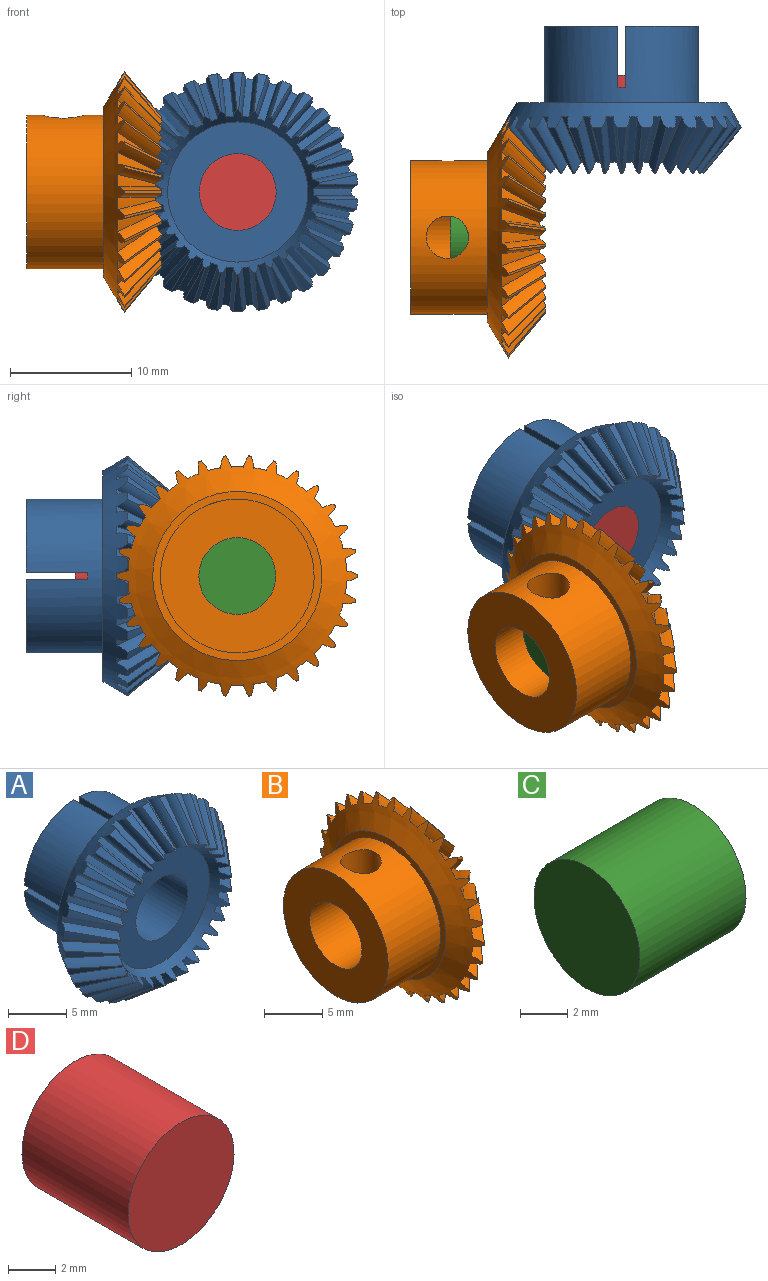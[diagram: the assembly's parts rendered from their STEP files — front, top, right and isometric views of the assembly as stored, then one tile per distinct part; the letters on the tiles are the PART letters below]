
ASSEMBLY  parts=4 mates=2
PART A: 142 faces, bbox 20.3x12.2x20.3 mm
  f0: cone r=8.72mm half-angle=30deg, axis (0,-1,0), area 108.7mm2, adj f4,f8,f9,f10,f11,f12,f13,f14
  f1: cone r=6.8mm half-angle=30deg, axis (0,-1,0), area 49.4mm2, adj f4,f8,f9,f10,f11,f12,f13,f14
  f2: cylinder r=3.17mm len=10.41mm, axis (0,1,0), area 194.7mm2, adj f5,f6,f7,f36,f37,f130,f131,f132
  f3: cylinder r=6.35mm len=12.7mm, axis (0,1,0), area 240.4mm2, adj f5,f6,f7,f36,f39,f130,f131,f132
  f4: cone r=9.91mm half-angle=39.7deg, axis (0,1,0), area 2.1mm2, adj f0,f1,f106,f111
  f5: plane 6.02x6.02mm, normal (0,1,0), area 21.7mm2, adj f2,f3,f137,f139
  f6: plane 6.02x6.02mm, normal (0,1,0), area 21.7mm2, adj f2,f3,f134,f136
  f7: plane 6.02x6.02mm, normal (0,1,0), area 21.7mm2, adj f2,f3,f131,f133
  f8: cone r=9.91mm half-angle=39.7deg, axis (0,1,0), area 2.1mm2, adj f0,f1,f42,f127
  f9: cone r=9.91mm half-angle=39.7deg, axis (0,1,0), area 2.1mm2, adj f0,f1,f124,f129
  f10: cone r=9.91mm half-angle=39.7deg, axis (0,1,0), area 2.1mm2, adj f0,f1,f121,f126
  f11: cone r=9.91mm half-angle=39.7deg, axis (0,1,0), area 2.1mm2, adj f0,f1,f118,f123
  f12: cone r=9.91mm half-angle=39.7deg, axis (0,1,0), area 2.1mm2, adj f0,f1,f115,f120
  f13: cone r=9.91mm half-angle=39.7deg, axis (0,1,0), area 2.1mm2, adj f0,f1,f112,f117
  f14: cone r=9.91mm half-angle=39.7deg, axis (0,1,0), area 2.1mm2, adj f0,f1,f109,f114
  f15: cone r=9.91mm half-angle=39.7deg, axis (0,1,0), area 2.1mm2, adj f0,f1,f103,f108
  f16: cone r=9.91mm half-angle=39.7deg, axis (0,1,0), area 2.1mm2, adj f0,f1,f100,f105
  f17: cone r=9.91mm half-angle=39.7deg, axis (0,1,0), area 2.1mm2, adj f0,f1,f97,f102
  f18: cone r=9.91mm half-angle=39.7deg, axis (0,1,0), area 2.1mm2, adj f0,f1,f94,f99
  f19: cone r=9.91mm half-angle=39.7deg, axis (0,1,0), area 2.1mm2, adj f0,f1,f91,f96
  f20: cone r=9.91mm half-angle=39.7deg, axis (0,1,0), area 2.1mm2, adj f0,f1,f88,f93
  f21: cone r=9.91mm half-angle=39.7deg, axis (0,1,0), area 2.1mm2, adj f0,f1,f85,f90
  f22: cone r=9.91mm half-angle=39.7deg, axis (0,1,0), area 2.1mm2, adj f0,f1,f82,f87
  f23: cone r=9.91mm half-angle=39.7deg, axis (0,1,0), area 2.1mm2, adj f0,f1,f79,f84
  f24: cone r=9.91mm half-angle=39.7deg, axis (0,1,0), area 2.1mm2, adj f0,f1,f76,f81
  f25: cone r=9.91mm half-angle=39.7deg, axis (0,1,0), area 2.1mm2, adj f0,f1,f73,f78
  f26: cone r=9.91mm half-angle=39.7deg, axis (0,1,0), area 2.1mm2, adj f0,f1,f70,f75
  f27: cone r=9.91mm half-angle=39.7deg, axis (0,1,0), area 2.1mm2, adj f0,f1,f67,f72
  f28: cone r=9.91mm half-angle=39.7deg, axis (0,1,0), area 2.1mm2, adj f0,f1,f64,f69
  f29: cone r=9.91mm half-angle=39.7deg, axis (0,1,0), area 2.1mm2, adj f0,f1,f61,f66
  f30: cone r=9.91mm half-angle=39.7deg, axis (0,1,0), area 2.1mm2, adj f0,f1,f58,f63
  f31: cone r=9.91mm half-angle=39.7deg, axis (0,1,0), area 2.1mm2, adj f0,f1,f55,f60
  f32: cone r=9.91mm half-angle=39.7deg, axis (0,1,0), area 2.1mm2, adj f0,f1,f52,f57
  f33: cone r=9.91mm half-angle=39.7deg, axis (0,1,0), area 2.1mm2, adj f0,f1,f49,f54
  f34: cone r=9.91mm half-angle=39.7deg, axis (0,1,0), area 2.1mm2, adj f0,f1,f46,f51
  f35: cone r=9.91mm half-angle=39.7deg, axis (0,1,0), area 2.1mm2, adj f0,f1,f43,f48
  f36: plane 6.02x6.02mm, normal (0,1,0), area 21.7mm2, adj f2,f3,f130,f140
  f37: plane 11.58x11.58mm, normal (0,-1,0), area 73.7mm2, adj f1,f2
  f38: cone r=9.91mm half-angle=39.7deg, axis (0,1,0), area 2.1mm2, adj f0,f1,f41,f45
  f39: plane 17.45x17.45mm, normal (0,1,0), area 112.4mm2, adj f0,f3
  f40: cylinder r=7.38mm len=3.75mm, axis (0.64,-0.77,0), area 3mm2, adj f0,f1,f41,f42
  f41: cylinder r=1.83mm len=4.68mm, axis (0.64,-0.77,0), area 5.2mm2, adj f0,f1,f38,f40
  f42: cylinder r=1.83mm len=4.68mm, axis (0.64,-0.77,0), area 5.2mm2, adj f0,f1,f8,f40
  f43: cylinder r=1.83mm len=4.68mm, axis (0.63,-0.77,0.13), area 5.2mm2, adj f0,f1,f35,f44
  f44: cylinder r=7.38mm len=3.75mm, axis (0.63,-0.77,0.13), area 3mm2, adj f0,f1,f43,f45
  f45: cylinder r=1.83mm len=4.68mm, axis (0.63,-0.77,0.13), area 5.2mm2, adj f0,f1,f38,f44
  f46: cylinder r=1.83mm len=4.68mm, axis (0.58,-0.77,0.26), area 5.2mm2, adj f0,f1,f34,f47
  f47: cylinder r=7.38mm len=3.75mm, axis (0.58,-0.77,0.26), area 3mm2, adj f0,f1,f46,f48
  f48: cylinder r=1.83mm len=4.68mm, axis (0.58,-0.77,0.26), area 5.2mm2, adj f0,f1,f35,f47
  f49: cylinder r=1.83mm len=4.68mm, axis (0.52,-0.77,0.38), area 5.2mm2, adj f0,f1,f33,f50
  f50: cylinder r=7.38mm len=3.75mm, axis (0.52,-0.77,0.38), area 3mm2, adj f0,f1,f49,f51
  f51: cylinder r=1.83mm len=4.68mm, axis (0.52,-0.77,0.38), area 5.2mm2, adj f0,f1,f34,f50
  f52: cylinder r=1.83mm len=4.68mm, axis (0.43,-0.77,0.48), area 5.2mm2, adj f0,f1,f32,f53
  f53: cylinder r=7.38mm len=3.75mm, axis (0.43,-0.77,0.48), area 3mm2, adj f0,f1,f52,f54
  f54: cylinder r=1.83mm len=4.68mm, axis (0.43,-0.77,0.48), area 5.2mm2, adj f0,f1,f33,f53
  f55: cylinder r=1.83mm len=4.68mm, axis (0.32,-0.77,0.55), area 5.2mm2, adj f0,f1,f31,f56
  f56: cylinder r=7.38mm len=3.75mm, axis (0.32,-0.77,0.55), area 3mm2, adj f0,f1,f55,f57
  f57: cylinder r=1.83mm len=4.68mm, axis (0.32,-0.77,0.55), area 5.2mm2, adj f0,f1,f32,f56
  f58: cylinder r=1.83mm len=4.68mm, axis (0.2,-0.77,0.61), area 5.2mm2, adj f0,f1,f30,f59
  f59: cylinder r=7.38mm len=3.75mm, axis (0.2,-0.77,0.61), area 3mm2, adj f0,f1,f58,f60
  f60: cylinder r=1.83mm len=4.68mm, axis (0.2,-0.77,0.61), area 5.2mm2, adj f0,f1,f31,f59
  f61: cylinder r=1.83mm len=4.68mm, axis (0.07,-0.77,0.64), area 5.2mm2, adj f0,f1,f29,f62
  f62: cylinder r=7.38mm len=3.75mm, axis (0.07,-0.77,0.64), area 3mm2, adj f0,f1,f61,f63
  f63: cylinder r=1.83mm len=4.68mm, axis (0.07,-0.77,0.64), area 5.2mm2, adj f0,f1,f30,f62
  f64: cylinder r=1.83mm len=4.68mm, axis (-0.07,-0.77,0.64), area 5.2mm2, adj f0,f1,f28,f65
  f65: cylinder r=7.38mm len=3.75mm, axis (-0.07,-0.77,0.64), area 3mm2, adj f0,f1,f64,f66
  f66: cylinder r=1.83mm len=4.68mm, axis (-0.07,-0.77,0.64), area 5.2mm2, adj f0,f1,f29,f65
  f67: cylinder r=1.83mm len=4.68mm, axis (-0.2,-0.77,0.61), area 5.2mm2, adj f0,f1,f27,f68
  f68: cylinder r=7.38mm len=3.75mm, axis (-0.2,-0.77,0.61), area 3mm2, adj f0,f1,f67,f69
  f69: cylinder r=1.83mm len=4.68mm, axis (-0.2,-0.77,0.61), area 5.2mm2, adj f0,f1,f28,f68
  f70: cylinder r=1.83mm len=4.68mm, axis (-0.32,-0.77,0.55), area 5.2mm2, adj f0,f1,f26,f71
  f71: cylinder r=7.38mm len=3.75mm, axis (-0.32,-0.77,0.55), area 3mm2, adj f0,f1,f70,f72
  f72: cylinder r=1.83mm len=4.68mm, axis (-0.32,-0.77,0.55), area 5.2mm2, adj f0,f1,f27,f71
  f73: cylinder r=1.83mm len=4.68mm, axis (-0.43,-0.77,0.48), area 5.2mm2, adj f0,f1,f25,f74
  f74: cylinder r=7.38mm len=3.75mm, axis (-0.43,-0.77,0.48), area 3mm2, adj f0,f1,f73,f75
  f75: cylinder r=1.83mm len=4.68mm, axis (-0.43,-0.77,0.48), area 5.2mm2, adj f0,f1,f26,f74
  f76: cylinder r=1.83mm len=4.68mm, axis (-0.52,-0.77,0.38), area 5.2mm2, adj f0,f1,f24,f77
  f77: cylinder r=7.38mm len=3.75mm, axis (-0.52,-0.77,0.38), area 3mm2, adj f0,f1,f76,f78
  f78: cylinder r=1.83mm len=4.68mm, axis (-0.52,-0.77,0.38), area 5.2mm2, adj f0,f1,f25,f77
  f79: cylinder r=1.83mm len=4.68mm, axis (-0.58,-0.77,0.26), area 5.2mm2, adj f0,f1,f23,f80
  f80: cylinder r=7.38mm len=3.75mm, axis (-0.58,-0.77,0.26), area 3mm2, adj f0,f1,f79,f81
  f81: cylinder r=1.83mm len=4.68mm, axis (-0.58,-0.77,0.26), area 5.2mm2, adj f0,f1,f24,f80
  f82: cylinder r=1.83mm len=4.68mm, axis (-0.63,-0.77,0.13), area 5.2mm2, adj f0,f1,f22,f83
  f83: cylinder r=7.38mm len=3.75mm, axis (-0.63,-0.77,0.13), area 3mm2, adj f0,f1,f82,f84
  f84: cylinder r=1.83mm len=4.68mm, axis (-0.63,-0.77,0.13), area 5.2mm2, adj f0,f1,f23,f83
  f85: cylinder r=1.83mm len=4.68mm, axis (-0.64,-0.77,0), area 5.2mm2, adj f0,f1,f21,f86
  f86: cylinder r=7.38mm len=3.75mm, axis (-0.64,-0.77,0), area 3mm2, adj f0,f1,f85,f87
  f87: cylinder r=1.83mm len=4.68mm, axis (-0.64,-0.77,0), area 5.2mm2, adj f0,f1,f22,f86
  f88: cylinder r=1.83mm len=4.68mm, axis (-0.63,-0.77,-0.13), area 5.2mm2, adj f0,f1,f20,f89
  f89: cylinder r=7.38mm len=3.75mm, axis (-0.63,-0.77,-0.13), area 3mm2, adj f0,f1,f88,f90
  f90: cylinder r=1.83mm len=4.68mm, axis (-0.63,-0.77,-0.13), area 5.2mm2, adj f0,f1,f21,f89
  f91: cylinder r=1.83mm len=4.68mm, axis (-0.58,-0.77,-0.26), area 5.2mm2, adj f0,f1,f19,f92
  f92: cylinder r=7.38mm len=3.75mm, axis (-0.58,-0.77,-0.26), area 3mm2, adj f0,f1,f91,f93
  f93: cylinder r=1.83mm len=4.68mm, axis (-0.58,-0.77,-0.26), area 5.2mm2, adj f0,f1,f20,f92
  f94: cylinder r=1.83mm len=4.68mm, axis (-0.52,-0.77,-0.38), area 5.2mm2, adj f0,f1,f18,f95
  f95: cylinder r=7.38mm len=3.75mm, axis (-0.52,-0.77,-0.38), area 3mm2, adj f0,f1,f94,f96
  f96: cylinder r=1.83mm len=4.68mm, axis (-0.52,-0.77,-0.38), area 5.2mm2, adj f0,f1,f19,f95
  f97: cylinder r=1.83mm len=4.68mm, axis (-0.43,-0.77,-0.48), area 5.2mm2, adj f0,f1,f17,f98
  f98: cylinder r=7.38mm len=3.75mm, axis (-0.43,-0.77,-0.48), area 3mm2, adj f0,f1,f97,f99
  f99: cylinder r=1.83mm len=4.68mm, axis (-0.43,-0.77,-0.48), area 5.2mm2, adj f0,f1,f18,f98
  f100: cylinder r=1.83mm len=4.68mm, axis (-0.32,-0.77,-0.55), area 5.2mm2, adj f0,f1,f16,f101
  f101: cylinder r=7.38mm len=3.75mm, axis (-0.32,-0.77,-0.55), area 3mm2, adj f0,f1,f100,f102
  f102: cylinder r=1.83mm len=4.68mm, axis (-0.32,-0.77,-0.55), area 5.2mm2, adj f0,f1,f17,f101
  f103: cylinder r=1.83mm len=4.68mm, axis (-0.2,-0.77,-0.61), area 5.2mm2, adj f0,f1,f15,f104
  f104: cylinder r=7.38mm len=3.75mm, axis (-0.2,-0.77,-0.61), area 3mm2, adj f0,f1,f103,f105
  f105: cylinder r=1.83mm len=4.68mm, axis (-0.2,-0.77,-0.61), area 5.2mm2, adj f0,f1,f16,f104
  f106: cylinder r=1.83mm len=4.68mm, axis (-0.07,-0.77,-0.64), area 5.2mm2, adj f0,f1,f4,f107
  f107: cylinder r=7.38mm len=3.75mm, axis (-0.07,-0.77,-0.64), area 3mm2, adj f0,f1,f106,f108
  f108: cylinder r=1.83mm len=4.68mm, axis (-0.07,-0.77,-0.64), area 5.2mm2, adj f0,f1,f15,f107
  f109: cylinder r=1.83mm len=4.68mm, axis (0.07,-0.77,-0.64), area 5.2mm2, adj f0,f1,f14,f110
  f110: cylinder r=7.38mm len=3.75mm, axis (0.07,-0.77,-0.64), area 3mm2, adj f0,f1,f109,f111
  f111: cylinder r=1.83mm len=4.68mm, axis (0.07,-0.77,-0.64), area 5.2mm2, adj f0,f1,f4,f110
  f112: cylinder r=1.83mm len=4.68mm, axis (0.2,-0.77,-0.61), area 5.2mm2, adj f0,f1,f13,f113
  f113: cylinder r=7.38mm len=3.75mm, axis (0.2,-0.77,-0.61), area 3mm2, adj f0,f1,f112,f114
  f114: cylinder r=1.83mm len=4.68mm, axis (0.2,-0.77,-0.61), area 5.2mm2, adj f0,f1,f14,f113
  f115: cylinder r=1.83mm len=4.68mm, axis (0.32,-0.77,-0.55), area 5.2mm2, adj f0,f1,f12,f116
  f116: cylinder r=7.38mm len=3.75mm, axis (0.32,-0.77,-0.55), area 3mm2, adj f0,f1,f115,f117
  f117: cylinder r=1.83mm len=4.68mm, axis (0.32,-0.77,-0.55), area 5.2mm2, adj f0,f1,f13,f116
  f118: cylinder r=1.83mm len=4.68mm, axis (0.43,-0.77,-0.48), area 5.2mm2, adj f0,f1,f11,f119
  f119: cylinder r=7.38mm len=3.75mm, axis (0.43,-0.77,-0.48), area 3mm2, adj f0,f1,f118,f120
  f120: cylinder r=1.83mm len=4.68mm, axis (0.43,-0.77,-0.48), area 5.2mm2, adj f0,f1,f12,f119
  f121: cylinder r=1.83mm len=4.68mm, axis (0.52,-0.77,-0.38), area 5.2mm2, adj f0,f1,f10,f122
  f122: cylinder r=7.38mm len=3.75mm, axis (0.52,-0.77,-0.38), area 3mm2, adj f0,f1,f121,f123
  f123: cylinder r=1.83mm len=4.68mm, axis (0.52,-0.77,-0.38), area 5.2mm2, adj f0,f1,f11,f122
  f124: cylinder r=1.83mm len=4.68mm, axis (0.58,-0.77,-0.26), area 5.2mm2, adj f0,f1,f9,f125
  f125: cylinder r=7.38mm len=3.75mm, axis (0.58,-0.77,-0.26), area 3mm2, adj f0,f1,f124,f126
  f126: cylinder r=1.83mm len=4.68mm, axis (0.58,-0.77,-0.26), area 5.2mm2, adj f0,f1,f10,f125
  f127: cylinder r=1.83mm len=4.68mm, axis (0.63,-0.77,-0.13), area 5.2mm2, adj f0,f1,f8,f128
  f128: cylinder r=7.38mm len=3.75mm, axis (0.63,-0.77,-0.13), area 3mm2, adj f0,f1,f127,f129
  f129: cylinder r=1.83mm len=4.68mm, axis (0.63,-0.77,-0.13), area 5.2mm2, adj f0,f1,f9,f128
  f130: plane 5.08x3.19mm, normal (-1,0,0), area 16.2mm2, adj f2,f3,f36,f132
  f131: plane 5.08x3.19mm, normal (1,0,0), area 16.2mm2, adj f2,f3,f7,f132
  f132: plane 3.19x0.64mm, normal (0,1,0), area 2mm2, adj f2,f3,f130,f131
  f133: plane 5.08x3.19mm, normal (0,0,-1), area 16.2mm2, adj f2,f3,f7,f135
  f134: plane 5.08x3.19mm, normal (0,0,1), area 16.2mm2, adj f2,f3,f6,f135
  f135: plane 3.19x0.64mm, normal (0,1,0), area 2mm2, adj f2,f3,f133,f134
  f136: plane 5.08x3.19mm, normal (1,0,0), area 16.2mm2, adj f2,f3,f6,f138
  f137: plane 5.08x3.19mm, normal (-1,0,0), area 16.2mm2, adj f2,f3,f5,f138
  f138: plane 3.19x0.64mm, normal (0,1,0), area 2mm2, adj f2,f3,f136,f137
  f139: plane 5.08x3.19mm, normal (0,0,1), area 16.2mm2, adj f2,f3,f5,f141
  f140: plane 5.08x3.19mm, normal (0,0,-1), area 16.2mm2, adj f2,f3,f36,f141
  f141: plane 3.19x0.64mm, normal (0,1,0), area 2mm2, adj f2,f3,f139,f140
PART B: 130 faces, bbox 11.4x19.9x19.9 mm
  f0: cone r=0.89mm half-angle=59deg, axis (0,1,0), area 2.9mm2, adj f1
  f1: cylinder r=0.89mm len=1.78mm, axis (0,1,0), area 2.5mm2, adj f0,f3
  f2: cylinder r=1.75mm len=3.51mm, axis (0,0,1), area 35mm2, adj f3,f4
  f3: cylinder r=6.35mm len=12.7mm, axis (-1,0,0), area 241.1mm2, adj f1,f2,f128,f129
  f4: cylinder r=3.17mm len=9.65mm, axis (-1,0,0), area 182.3mm2, adj f2,f127,f128
  f5: cone r=3.55mm half-angle=60deg, axis (1,0,0), area 74.1mm2, adj f7,f8,f9,f10,f11,f12,f13,f14
  f6: cone r=9.04mm half-angle=60deg, axis (1,0,0), area 138.5mm2, adj f7,f8,f9,f10,f11,f12,f13,f14
  f7: cone r=5.29mm half-angle=50.3deg, axis (-1,0,0), area 2.9mm2, adj f5,f6,f53,f54
  f8: cylinder r=7.38mm len=3.71mm, axis (0.64,-0.75,0.16), area 1mm2, adj f5,f6,f96,f97
  f9: cylinder r=7.38mm len=3.51mm, axis (0.64,-0.7,0.31), area 1mm2, adj f5,f6,f94,f95
  f10: cylinder r=7.38mm len=3.15mm, axis (0.64,-0.62,0.45), area 1mm2, adj f5,f6,f92,f93
  f11: cylinder r=7.38mm len=3.12mm, axis (0.64,-0.51,0.57), area 1mm2, adj f5,f6,f90,f91
  f12: cylinder r=7.38mm len=3.35mm, axis (0.64,-0.38,0.67), area 1mm2, adj f5,f6,f88,f89
  f13: cylinder r=7.38mm len=3.63mm, axis (0.64,-0.24,0.73), area 1mm2, adj f5,f6,f86,f87
  f14: cylinder r=7.38mm len=3.75mm, axis (0.64,-0.08,0.76), area 1mm2, adj f5,f6,f84,f85
  f15: cylinder r=7.38mm len=3.75mm, axis (0.64,0.08,0.76), area 1mm2, adj f5,f6,f82,f83
  f16: cylinder r=7.38mm len=3.63mm, axis (0.64,0.24,0.73), area 1mm2, adj f5,f6,f80,f81
  f17: cylinder r=7.38mm len=3.35mm, axis (0.64,0.38,0.67), area 1mm2, adj f5,f6,f78,f79
  f18: cylinder r=7.38mm len=3.12mm, axis (0.64,0.51,0.57), area 1mm2, adj f5,f6,f76,f77
  f19: cylinder r=7.38mm len=3.15mm, axis (0.64,0.62,0.45), area 1mm2, adj f5,f6,f74,f75
  f20: cylinder r=7.38mm len=3.51mm, axis (0.64,0.7,0.31), area 1mm2, adj f5,f6,f72,f73
  f21: cylinder r=7.38mm len=3.71mm, axis (0.64,0.75,0.16), area 1mm2, adj f5,f6,f70,f71
  f22: cylinder r=7.38mm len=3.75mm, axis (0.64,0.77,0), area 1mm2, adj f5,f6,f68,f69
  f23: cylinder r=7.38mm len=3.71mm, axis (0.64,0.75,-0.16), area 1mm2, adj f5,f6,f66,f67
  f24: cylinder r=7.38mm len=3.51mm, axis (0.64,0.7,-0.31), area 1mm2, adj f5,f6,f64,f65
  f25: cylinder r=7.38mm len=3.15mm, axis (0.64,0.62,-0.45), area 1mm2, adj f5,f6,f62,f63
  f26: cylinder r=7.38mm len=3.12mm, axis (0.64,0.51,-0.57), area 1mm2, adj f5,f6,f60,f61
  f27: cylinder r=7.38mm len=3.35mm, axis (0.64,0.38,-0.67), area 1mm2, adj f5,f6,f58,f59
  f28: cylinder r=7.38mm len=3.63mm, axis (0.64,0.24,-0.73), area 1mm2, adj f5,f6,f56,f57
  f29: cylinder r=7.38mm len=3.75mm, axis (0.64,0.08,-0.76), area 1mm2, adj f5,f6,f54,f55
  f30: cylinder r=7.38mm len=3.75mm, axis (0.64,-0.08,-0.76), area 1mm2, adj f5,f6,f52,f53
  f31: cylinder r=7.38mm len=3.63mm, axis (0.64,-0.24,-0.73), area 1mm2, adj f5,f6,f50,f51
  f32: cylinder r=7.38mm len=3.35mm, axis (0.64,-0.38,-0.67), area 1mm2, adj f5,f6,f48,f49
  f33: cylinder r=7.38mm len=3.12mm, axis (0.64,-0.51,-0.57), area 1mm2, adj f5,f6,f46,f47
  f34: cylinder r=7.38mm len=3.15mm, axis (0.64,-0.62,-0.45), area 1mm2, adj f5,f6,f44,f45
  f35: cylinder r=7.38mm len=3.51mm, axis (0.64,-0.7,-0.31), area 1mm2, adj f5,f6,f42,f43
  f36: cylinder r=7.38mm len=3.71mm, axis (0.64,-0.75,-0.16), area 1mm2, adj f5,f6,f40,f41
  f37: cylinder r=7.38mm len=3.75mm, axis (0.64,-0.77,0), area 1mm2, adj f5,f6,f38,f39
  f38: cylinder r=3.19mm len=4.69mm, axis (0.64,-0.77,0), area 5.2mm2, adj f5,f6,f37,f126
  f39: cylinder r=3.19mm len=4.69mm, axis (0.64,-0.77,0), area 5.2mm2, adj f5,f6,f37,f98
  f40: cylinder r=3.19mm len=4.52mm, axis (0.64,-0.75,-0.16), area 5.2mm2, adj f5,f6,f36,f98
  f41: cylinder r=3.19mm len=4.65mm, axis (0.64,-0.75,-0.16), area 5.2mm2, adj f5,f6,f36,f99
  f42: cylinder r=3.19mm len=4.15mm, axis (0.64,-0.7,-0.31), area 5.2mm2, adj f5,f6,f35,f99
  f43: cylinder r=3.19mm len=4.42mm, axis (0.64,-0.7,-0.31), area 5.2mm2, adj f5,f6,f35,f100
  f44: cylinder r=3.19mm len=4.14mm, axis (0.64,-0.62,-0.45), area 5.2mm2, adj f5,f6,f34,f100
  f45: cylinder r=3.19mm len=4.14mm, axis (0.64,-0.62,-0.45), area 5.2mm2, adj f5,f6,f34,f101
  f46: cylinder r=3.19mm len=4.14mm, axis (0.64,-0.51,-0.57), area 5.2mm2, adj f5,f6,f33,f101
  f47: cylinder r=3.19mm len=4.14mm, axis (0.64,-0.51,-0.57), area 5.2mm2, adj f5,f6,f33,f102
  f48: cylinder r=3.19mm len=4.22mm, axis (0.64,-0.38,-0.67), area 5.2mm2, adj f5,f6,f32,f102
  f49: cylinder r=3.19mm len=4.14mm, axis (0.64,-0.38,-0.67), area 5.2mm2, adj f5,f6,f32,f103
  f50: cylinder r=3.19mm len=4.56mm, axis (0.64,-0.24,-0.73), area 5.2mm2, adj f5,f6,f31,f103
  f51: cylinder r=3.19mm len=4.36mm, axis (0.64,-0.24,-0.73), area 5.2mm2, adj f5,f6,f31,f104
  f52: cylinder r=3.19mm len=4.7mm, axis (0.64,-0.08,-0.76), area 5.2mm2, adj f5,f6,f30,f104
  f53: cylinder r=3.19mm len=4.63mm, axis (0.64,-0.08,-0.76), area 5.2mm2, adj f5,f6,f7,f30
  f54: cylinder r=3.19mm len=4.63mm, axis (0.64,0.08,-0.76), area 5.2mm2, adj f5,f6,f7,f29
  f55: cylinder r=3.19mm len=4.7mm, axis (0.64,0.08,-0.76), area 5.2mm2, adj f5,f6,f29,f105
  f56: cylinder r=3.19mm len=4.36mm, axis (0.64,0.24,-0.73), area 5.2mm2, adj f5,f6,f28,f105
  f57: cylinder r=3.19mm len=4.56mm, axis (0.64,0.24,-0.73), area 5.2mm2, adj f5,f6,f28,f106
  f58: cylinder r=3.19mm len=4.14mm, axis (0.64,0.38,-0.67), area 5.2mm2, adj f5,f6,f27,f106
  f59: cylinder r=3.19mm len=4.22mm, axis (0.64,0.38,-0.67), area 5.2mm2, adj f5,f6,f27,f107
  f60: cylinder r=3.19mm len=4.14mm, axis (0.64,0.51,-0.57), area 5.2mm2, adj f5,f6,f26,f107
  f61: cylinder r=3.19mm len=4.14mm, axis (0.64,0.51,-0.57), area 5.2mm2, adj f5,f6,f26,f108
  f62: cylinder r=3.19mm len=4.14mm, axis (0.64,0.62,-0.45), area 5.2mm2, adj f5,f6,f25,f108
  f63: cylinder r=3.19mm len=4.14mm, axis (0.64,0.62,-0.45), area 5.2mm2, adj f5,f6,f25,f109
  f64: cylinder r=3.19mm len=4.42mm, axis (0.64,0.7,-0.31), area 5.2mm2, adj f5,f6,f24,f109
  f65: cylinder r=3.19mm len=4.15mm, axis (0.64,0.7,-0.31), area 5.2mm2, adj f5,f6,f24,f110
  f66: cylinder r=3.19mm len=4.65mm, axis (0.64,0.75,-0.16), area 5.2mm2, adj f5,f6,f23,f110
  f67: cylinder r=3.19mm len=4.52mm, axis (0.64,0.75,-0.16), area 5.2mm2, adj f5,f6,f23,f111
  f68: cylinder r=3.19mm len=4.69mm, axis (0.64,0.77,0), area 5.2mm2, adj f5,f6,f22,f111
  f69: cylinder r=3.19mm len=4.69mm, axis (0.64,0.77,0), area 5.2mm2, adj f5,f6,f22,f112
  f70: cylinder r=3.19mm len=4.52mm, axis (0.64,0.75,0.16), area 5.2mm2, adj f5,f6,f21,f112
  f71: cylinder r=3.19mm len=4.65mm, axis (0.64,0.75,0.16), area 5.2mm2, adj f5,f6,f21,f113
  f72: cylinder r=3.19mm len=4.15mm, axis (0.64,0.7,0.31), area 5.2mm2, adj f5,f6,f20,f113
  f73: cylinder r=3.19mm len=4.42mm, axis (0.64,0.7,0.31), area 5.2mm2, adj f5,f6,f20,f114
  f74: cylinder r=3.19mm len=4.14mm, axis (0.64,0.62,0.45), area 5.2mm2, adj f5,f6,f19,f114
  f75: cylinder r=3.19mm len=4.14mm, axis (0.64,0.62,0.45), area 5.2mm2, adj f5,f6,f19,f115
  f76: cylinder r=3.19mm len=4.14mm, axis (0.64,0.51,0.57), area 5.2mm2, adj f5,f6,f18,f115
  f77: cylinder r=3.19mm len=4.14mm, axis (0.64,0.51,0.57), area 5.2mm2, adj f5,f6,f18,f116
  f78: cylinder r=3.19mm len=4.22mm, axis (0.64,0.38,0.67), area 5.2mm2, adj f5,f6,f17,f116
  f79: cylinder r=3.19mm len=4.14mm, axis (0.64,0.38,0.67), area 5.2mm2, adj f5,f6,f17,f117
  f80: cylinder r=3.19mm len=4.56mm, axis (0.64,0.24,0.73), area 5.2mm2, adj f5,f6,f16,f117
  f81: cylinder r=3.19mm len=4.36mm, axis (0.64,0.24,0.73), area 5.2mm2, adj f5,f6,f16,f118
  f82: cylinder r=3.19mm len=4.7mm, axis (0.64,0.08,0.76), area 5.2mm2, adj f5,f6,f15,f118
  f83: cylinder r=3.19mm len=4.63mm, axis (0.64,0.08,0.76), area 5.2mm2, adj f5,f6,f15,f119
  f84: cylinder r=3.19mm len=4.63mm, axis (0.64,-0.08,0.76), area 5.2mm2, adj f5,f6,f14,f119
  f85: cylinder r=3.19mm len=4.7mm, axis (0.64,-0.08,0.76), area 5.2mm2, adj f5,f6,f14,f120
  f86: cylinder r=3.19mm len=4.36mm, axis (0.64,-0.24,0.73), area 5.2mm2, adj f5,f6,f13,f120
  f87: cylinder r=3.19mm len=4.56mm, axis (0.64,-0.24,0.73), area 5.2mm2, adj f5,f6,f13,f121
  f88: cylinder r=3.19mm len=4.14mm, axis (0.64,-0.38,0.67), area 5.2mm2, adj f5,f6,f12,f121
  f89: cylinder r=3.19mm len=4.22mm, axis (0.64,-0.38,0.67), area 5.2mm2, adj f5,f6,f12,f122
  f90: cylinder r=3.19mm len=4.14mm, axis (0.64,-0.51,0.57), area 5.2mm2, adj f5,f6,f11,f122
  f91: cylinder r=3.19mm len=4.14mm, axis (0.64,-0.51,0.57), area 5.2mm2, adj f5,f6,f11,f123
  f92: cylinder r=3.19mm len=4.14mm, axis (0.64,-0.62,0.45), area 5.2mm2, adj f5,f6,f10,f123
  f93: cylinder r=3.19mm len=4.14mm, axis (0.64,-0.62,0.45), area 5.2mm2, adj f5,f6,f10,f124
  f94: cylinder r=3.19mm len=4.42mm, axis (0.64,-0.7,0.31), area 5.2mm2, adj f5,f6,f9,f124
  f95: cylinder r=3.19mm len=4.15mm, axis (0.64,-0.7,0.31), area 5.2mm2, adj f5,f6,f9,f125
  f96: cylinder r=3.19mm len=4.65mm, axis (0.64,-0.75,0.16), area 5.2mm2, adj f5,f6,f8,f125
  f97: cylinder r=3.19mm len=4.52mm, axis (0.64,-0.75,0.16), area 5.2mm2, adj f5,f6,f8,f126
  f98: cone r=5.29mm half-angle=50.3deg, axis (-1,0,0), area 2.9mm2, adj f5,f6,f39,f40
  f99: cone r=5.29mm half-angle=50.3deg, axis (-1,0,0), area 2.9mm2, adj f5,f6,f41,f42
  f100: cone r=5.29mm half-angle=50.3deg, axis (-1,0,0), area 2.9mm2, adj f5,f6,f43,f44
  f101: cone r=5.29mm half-angle=50.3deg, axis (-1,0,0), area 2.9mm2, adj f5,f6,f45,f46
  f102: cone r=5.29mm half-angle=50.3deg, axis (-1,0,0), area 2.9mm2, adj f5,f6,f47,f48
  f103: cone r=5.29mm half-angle=50.3deg, axis (-1,0,0), area 2.9mm2, adj f5,f6,f49,f50
  f104: cone r=5.29mm half-angle=50.3deg, axis (-1,0,0), area 2.9mm2, adj f5,f6,f51,f52
  f105: cone r=5.29mm half-angle=50.3deg, axis (-1,0,0), area 2.9mm2, adj f5,f6,f55,f56
  f106: cone r=5.29mm half-angle=50.3deg, axis (-1,0,0), area 2.9mm2, adj f5,f6,f57,f58
  f107: cone r=5.29mm half-angle=50.3deg, axis (-1,0,0), area 2.9mm2, adj f5,f6,f59,f60
  f108: cone r=5.29mm half-angle=50.3deg, axis (-1,0,0), area 2.9mm2, adj f5,f6,f61,f62
  f109: cone r=5.29mm half-angle=50.3deg, axis (-1,0,0), area 2.9mm2, adj f5,f6,f63,f64
  f110: cone r=5.29mm half-angle=50.3deg, axis (-1,0,0), area 2.9mm2, adj f5,f6,f65,f66
  f111: cone r=5.29mm half-angle=50.3deg, axis (-1,0,0), area 2.9mm2, adj f5,f6,f67,f68
  f112: cone r=5.29mm half-angle=50.3deg, axis (-1,0,0), area 2.9mm2, adj f5,f6,f69,f70
  f113: cone r=5.29mm half-angle=50.3deg, axis (-1,0,0), area 2.9mm2, adj f5,f6,f71,f72
  f114: cone r=5.29mm half-angle=50.3deg, axis (-1,0,0), area 2.9mm2, adj f5,f6,f73,f74
  f115: cone r=5.29mm half-angle=50.3deg, axis (-1,0,0), area 2.9mm2, adj f5,f6,f75,f76
  f116: cone r=5.29mm half-angle=50.3deg, axis (-1,0,0), area 2.9mm2, adj f5,f6,f77,f78
  f117: cone r=5.29mm half-angle=50.3deg, axis (-1,0,0), area 2.9mm2, adj f5,f6,f79,f80
  f118: cone r=5.29mm half-angle=50.3deg, axis (-1,0,0), area 2.9mm2, adj f5,f6,f81,f82
  f119: cone r=5.29mm half-angle=50.3deg, axis (-1,0,0), area 2.9mm2, adj f5,f6,f83,f84
  f120: cone r=5.29mm half-angle=50.3deg, axis (-1,0,0), area 2.9mm2, adj f5,f6,f85,f86
  f121: cone r=5.29mm half-angle=50.3deg, axis (-1,0,0), area 2.9mm2, adj f5,f6,f87,f88
  f122: cone r=5.29mm half-angle=50.3deg, axis (-1,0,0), area 2.9mm2, adj f5,f6,f89,f90
  f123: cone r=5.29mm half-angle=50.3deg, axis (-1,0,0), area 2.9mm2, adj f5,f6,f91,f92
  f124: cone r=5.29mm half-angle=50.3deg, axis (-1,0,0), area 2.9mm2, adj f5,f6,f93,f94
  f125: cone r=5.29mm half-angle=50.3deg, axis (-1,0,0), area 2.9mm2, adj f5,f6,f95,f96
  f126: cone r=5.29mm half-angle=50.3deg, axis (-1,0,0), area 2.9mm2, adj f5,f6,f38,f97
  f127: plane 7.11x7.11mm, normal (1,0,0), area 8.1mm2, adj f4,f5
  f128: plane 12.7x12.7mm, normal (-1,0,0), area 95.1mm2, adj f3,f4
  f129: plane 13.97x13.97mm, normal (-1,0,0), area 26.6mm2, adj f3,f6
PART C: 3 faces, bbox 6.4x6.3x6.3 mm
  f0: cylinder r=3.17mm len=6.35mm, axis (1,0,0), area 126.6mm2, adj f1,f2
  f1: plane 6.35x6.35mm, normal (-1,0,0), area 31.6mm2, adj f0
  f2: plane 6.35x6.35mm, normal (1,0,0), area 31.6mm2, adj f0
PART D: 3 faces, bbox 6.3x6.4x6.3 mm
  f0: cylinder r=3.17mm len=6.35mm, axis (0,-1,0), area 126.6mm2, adj f1,f2
  f1: plane 6.35x6.35mm, normal (0,1,0), area 31.6mm2, adj f0
  f2: plane 6.35x6.35mm, normal (0,-1,0), area 31.6mm2, adj f0
PLACE A at identity
PLACE B at identity
PLACE C at identity fixed
PLACE D at identity fixed
MATE revolute A.f0 <-> D.f0  axis (0,-1,0) through (0,7.04,0)mm
MATE revolute B.f3 <-> C.f0  axis (1,0,0) through (-7.8,0,0)mm
